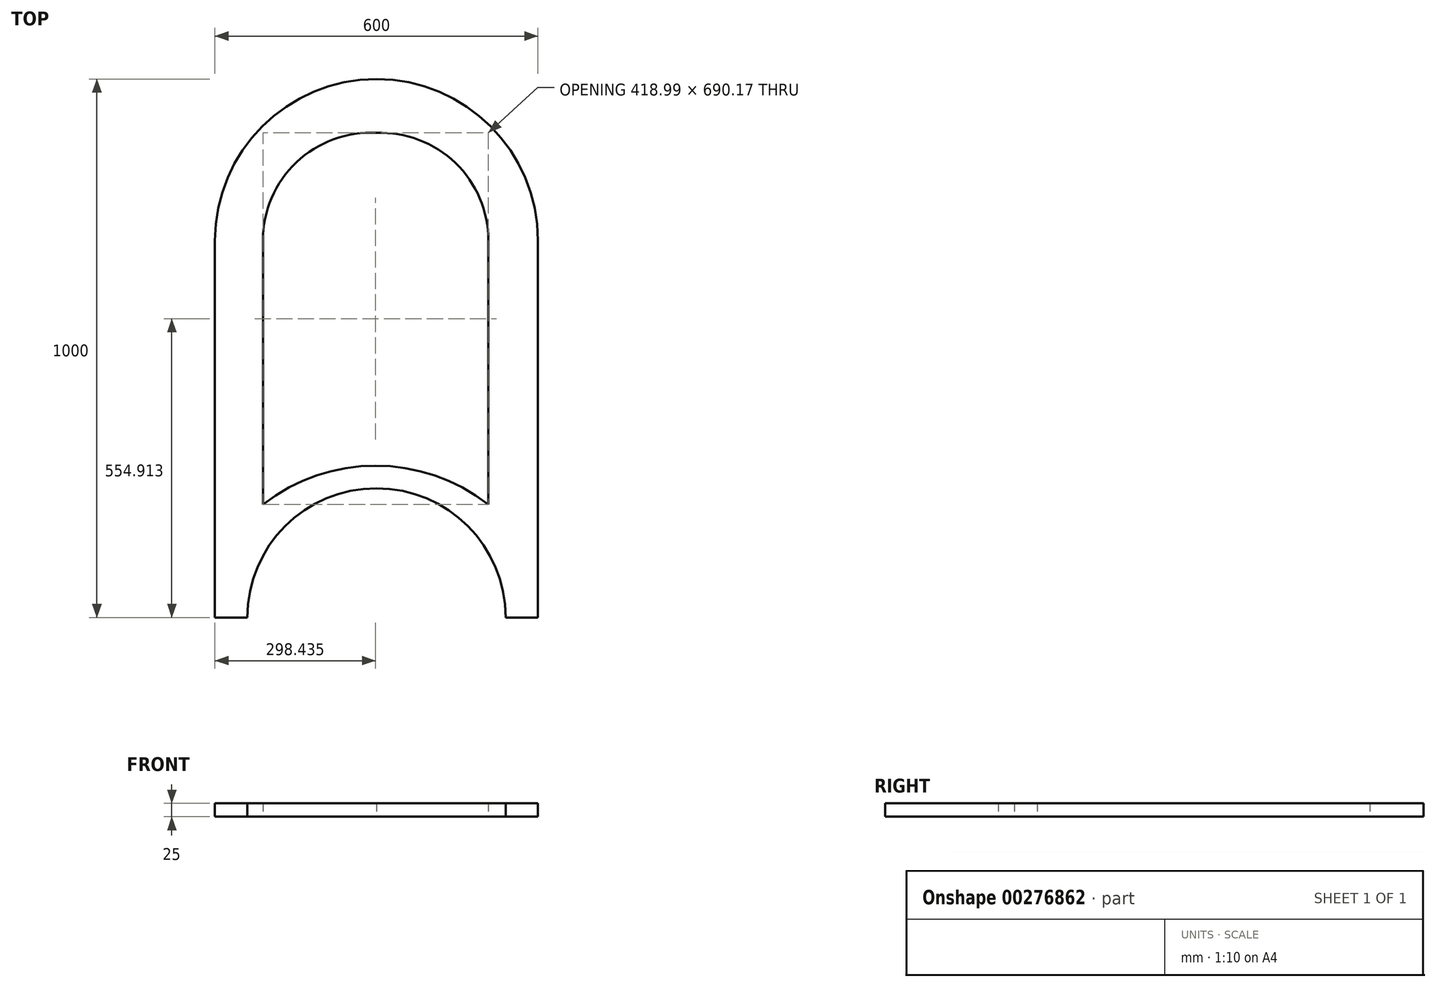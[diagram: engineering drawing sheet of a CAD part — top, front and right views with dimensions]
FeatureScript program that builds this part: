
annotation { "Feature Type Name" : "Feature", "Feature Type Description" : "" }
export const myFeature = defineFeature(function(context is Context, id is Id, definition is map)
    precondition{}
    {
        {
            var Q0;
            Q0=qCreatedBy(makeId("Top.planeOp"),FACE);
            var sketch = newSketch(context, id + "F0", { "sketchPlane" : qUnion([Q0])});
            skLineSegment(sketch, "E0", {"start": v(-88.94, -209.83) * mm, "end": v(-88.94, 490.17) * mm});
            skLineSegment(sketch, "E1", {"start": v(211.06, 790.17) * mm, "end": v(211.06, 790.17) * mm});
            skLineSegment(sketch, "E2", {"start": v(511.06, 490.17) * mm, "end": v(511.06, -209.83) * mm});
            skLineSegment(sketch, "E3", {"start": v(511.06, -209.83) * mm, "end": v(451.06, -209.83) * mm});
            skPoint(sketch, "E4.visualSharp", {"position": v(-88.94, 790.17) * mm});
            skArc(sketch, "E4.filletArc", {"start": v(211.06, 790.17) * mm, "mid": v(-1.07, 702.3) * mm, "end": v(-88.94, 490.17) * mm});
            skPoint(sketch, "E5.visualSharp", {"position": v(511.06, 790.17) * mm});
            skArc(sketch, "E5.filletArc", {"start": v(511.06, 490.17) * mm, "mid": v(423.2, 702.3) * mm, "end": v(211.06, 790.17) * mm});
            skArc(sketch, "E6", {"start": v(211.06, 690.17) * mm, "mid": v(62.43, 635.65) * mm, "end": v(0, 490.17) * mm});
            skArc(sketch, "E7", {"start": v(419, 490.17) * mm, "mid": v(357.64, 634.47) * mm, "end": v(211.06, 690.17) * mm});
            skLineSegment(sketch, "E8", {"start": v(0, 490.17) * mm, "end": v(0, 0) * mm});
            skLineSegment(sketch, "E9", {"start": v(419, 490.17) * mm, "end": v(419, 0) * mm});
            skArc(sketch, "E10", {"start": v(419, 0) * mm, "mid": v(209.5, 72.2) * mm, "end": v(0, 0) * mm});
            skArc(sketch, "E11", {"start": v(451.06, -209.83) * mm, "mid": v(211.06, 30.17) * mm, "end": v(-28.94, -209.83) * mm});
            skLineSegment(sketch, "E12.trimOffspring", {"start": v(-28.94, -209.83) * mm, "end": v(-88.94, -209.83) * mm});
            skSolve(sketch);
        }
        {
            var Q0;
            Q0 = qSketchRegion(id + "F0", true);
            extrude(context, id + "F1", {"entities" : qUnion([Q0]), "depth" : 25 * mm});
        }
    });
